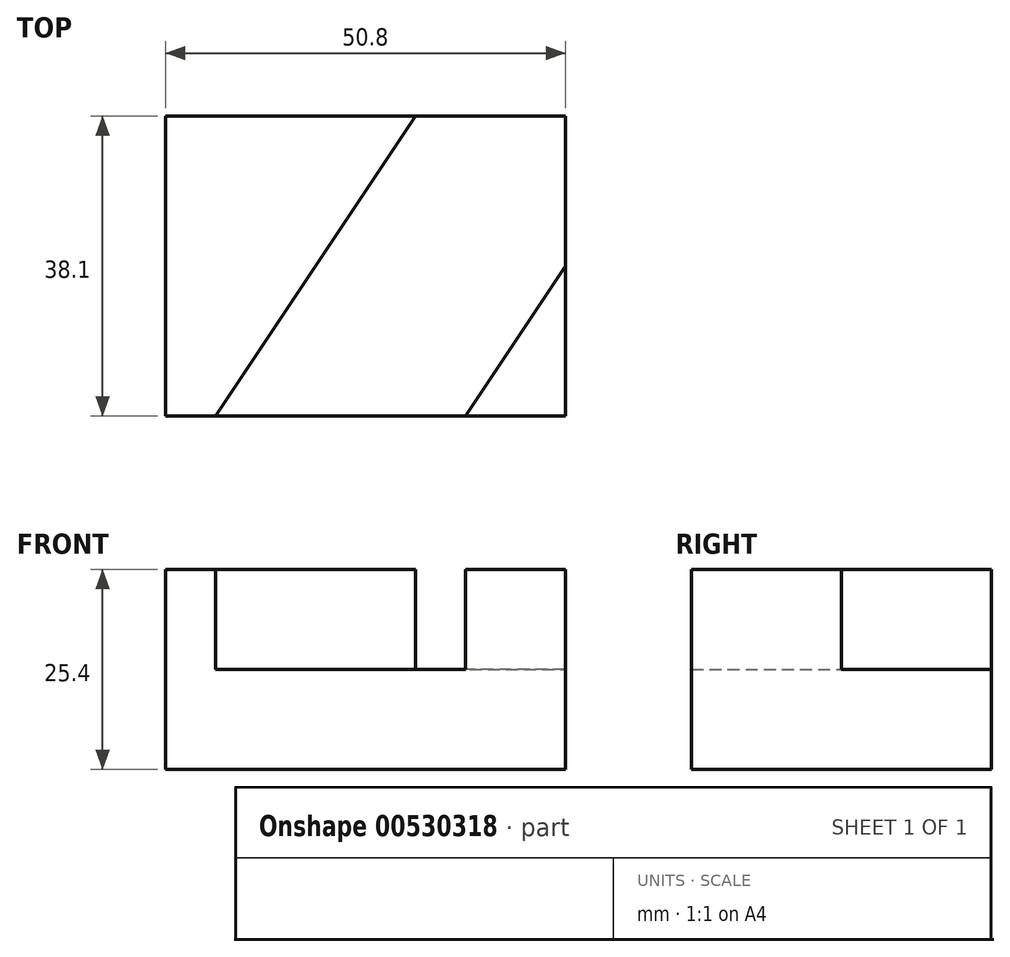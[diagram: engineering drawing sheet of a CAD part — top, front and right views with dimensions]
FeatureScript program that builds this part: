
annotation { "Feature Type Name" : "Feature", "Feature Type Description" : "" }
export const myFeature = defineFeature(function(context is Context, id is Id, definition is map)
    precondition{}
    {
        {
            var Q0;
            Q0=qCreatedBy(makeId("Front.planeOp"),FACE);
            var sketch = newSketch(context, id + "F0", { "sketchPlane" : qUnion([Q0])});
            skLineSegment(sketch, "E0.bottom", {"start": v(-69.12, 42.76) * mm, "end": v(-18.32, 42.76) * mm});
            skLineSegment(sketch, "E0.top", {"start": v(-69.12, 17.36) * mm, "end": v(-18.32, 17.36) * mm});
            skLineSegment(sketch, "E0.left", {"start": v(-69.12, 42.76) * mm, "end": v(-69.12, 17.36) * mm});
            skLineSegment(sketch, "E0.right", {"start": v(-18.32, 42.76) * mm, "end": v(-18.32, 17.36) * mm});
            skSolve(sketch);
        }
        {
            var Q0;
            Q0=makeQuery(id+"F0.imprint","IMPRINT",FACE,{"disambiguationData":[TD([[makeQuery(id+"F0.imprint","IMPRINT",EDGE,{"derivedFrom":sQuery(id+"F0.wireOp",EDGE,"E0.bottom")}),-1.0]])]});
            extrude(context, id + "F1", {"entities" : qUnion([Q0]), "depth" : 38.1 * mm, "offsetDistance" : 25.4 * mm});
        }
        {
            var Q0;
            Q0=makeQuery(id+"F1.opExtrude","SWEPT_FACE",FACE,{"disambiguationData":[OSD([sQuery(id+"F0.wireOp",EDGE,"E0.bottom")])]});
            var sketch = newSketch(context, id + "F2", { "sketchPlane" : qUnion([Q0])});
            skLineSegment(sketch, "E1", {"start": v(-69.12, -38.1) * mm, "end": v(-62.77, -38.1) * mm});
            skLineSegment(sketch, "E2", {"start": v(-18.32, 0) * mm, "end": v(-37.37, 0) * mm});
            skLineSegment(sketch, "E3", {"start": v(-62.77, -38.1) * mm, "end": v(-37.37, 0) * mm});
            skLineSegment(sketch, "E4", {"start": v(-62.77, -38.1) * mm, "end": v(-31.02, -38.1) * mm});
            skLineSegment(sketch, "E5", {"start": v(-31.02, -38.1) * mm, "end": v(-18.32, -38.1) * mm});
            skLineSegment(sketch, "E6", {"start": v(-18.32, -38.1) * mm, "end": v(-18.32, -19.05) * mm});
            skLineSegment(sketch, "E7", {"start": v(-18.32, -19.05) * mm, "end": v(-31.02, -38.1) * mm});
            skSolve(sketch);
        }
        {
            var Q0;
            {var subQ1=sQuery(id+"F2.wireOp",EDGE,"E2");Q0=makeQuery(id+"F2.imprint","IMPRINT",FACE,{"disambiguationData":[TD([[makeQuery(id+"F2.imprint","IMPRINT",EDGE,{"derivedFrom":subQ1}),-1.0]])]});}
            extrude(context, id + "F3", {"entities" : qUnion([Q0]), "operationType" : NewBodyOperationType.REMOVE, "oppositeDirection" : true, "depth" : 12.7 * mm, "offsetDistance" : 25.4 * mm});
        }
    });
